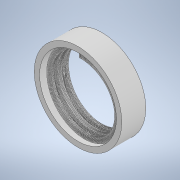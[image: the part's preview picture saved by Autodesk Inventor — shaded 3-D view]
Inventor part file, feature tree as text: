
AUTODESK INVENTOR PART (.ipt)
format: ipt  version: 2022 (Build 260153000, 153)  size: 253,952 bytes
history: native  units: mm
features: other x2, extrude x1, sketch x1
ambient origin geometry x8: Origin, YZ Plane, XZ Plane, XY Plane, X Axis, Y Axis, Z Axis, Center Point
bodies: Solid1 (feature_tree)
feature tree (4):
  other  "vial thread insert"
  extrude  "Extrusion1"  Depth=9.0mm TaperAngle=0.0deg
  sketch  "Sketch1"  dims[d0=2.0mm d1=9.0mm d2=0.0mm]
  other  "MeshFeature1"
